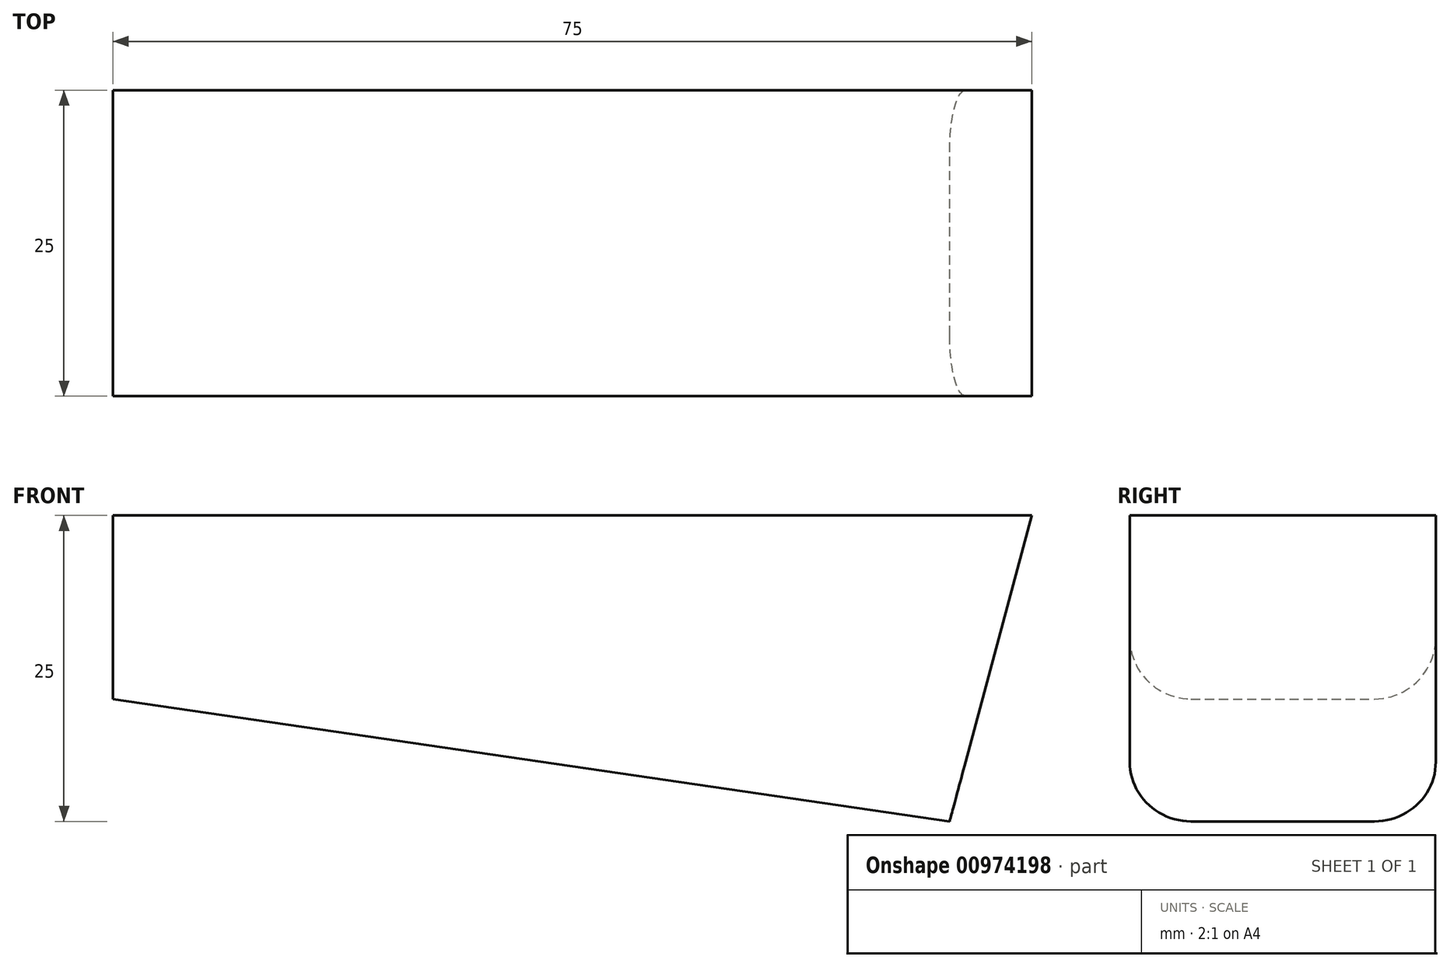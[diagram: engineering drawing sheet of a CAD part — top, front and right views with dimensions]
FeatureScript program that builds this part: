
annotation { "Feature Type Name" : "Feature", "Feature Type Description" : "" }
export const myFeature = defineFeature(function(context is Context, id is Id, definition is map)
    precondition{}
    {
        {
            var Q0;
            Q0=qCreatedBy(makeId("Front.planeOp"),FACE);
            var sketch = newSketch(context, id + "F0", { "sketchPlane" : qUnion([Q0])});
            skLineSegment(sketch, "E0", {"start": v(0, 0) * mm, "end": v(-75, 0) * mm});
            skLineSegment(sketch, "E1", {"start": v(-75, 0) * mm, "end": v(-75, -15) * mm});
            skLineSegment(sketch, "E2", {"start": v(0, 0) * mm, "end": v(0, -25) * mm, "construction": true});
            skLineSegment(sketch, "E3", {"start": v(0, -25) * mm, "end": v(-36.86, -25) * mm, "construction": true});
            skLineSegment(sketch, "E4", {"start": v(-6.7, -25) * mm, "end": v(-9.66, -36.04) * mm, "construction": true});
            skLineSegment(sketch, "E5", {"start": v(0, 0) * mm, "end": v(-6.7, -25) * mm});
            skLineSegment(sketch, "E6", {"start": v(-75, -15) * mm, "end": v(-6.7, -25) * mm});
            skSolve(sketch);
        }
        {
            var Q0;
            Q0 = qSketchRegion(id + "F0", true);
            extrude(context, id + "F1", {"entities" : qUnion([Q0]), "depth" : 25 * mm, "offsetDistance" : 25 * mm});
        }
        {
            var Q0;
            Q0=makeQuery(id+"F1.opExtrude","CAP_EDGE",EDGE,{"disambiguationData":[OSD([sQuery(id+"F0.wireOp",EDGE,"E6")])],"isStart":false});
            var Q1;
            Q1=makeQuery(id+"F1.opExtrude","CAP_EDGE",EDGE,{"disambiguationData":[OSD([sQuery(id+"F0.wireOp",EDGE,"E6")])],"isStart":true});
            fillet(context, id + "F2", {"entities" : qUnion([Q0, Q1]), "radius" : 5 * mm, "tangentPropagation" : true, "allowEdgeOverflow" : false});
        }
    });
